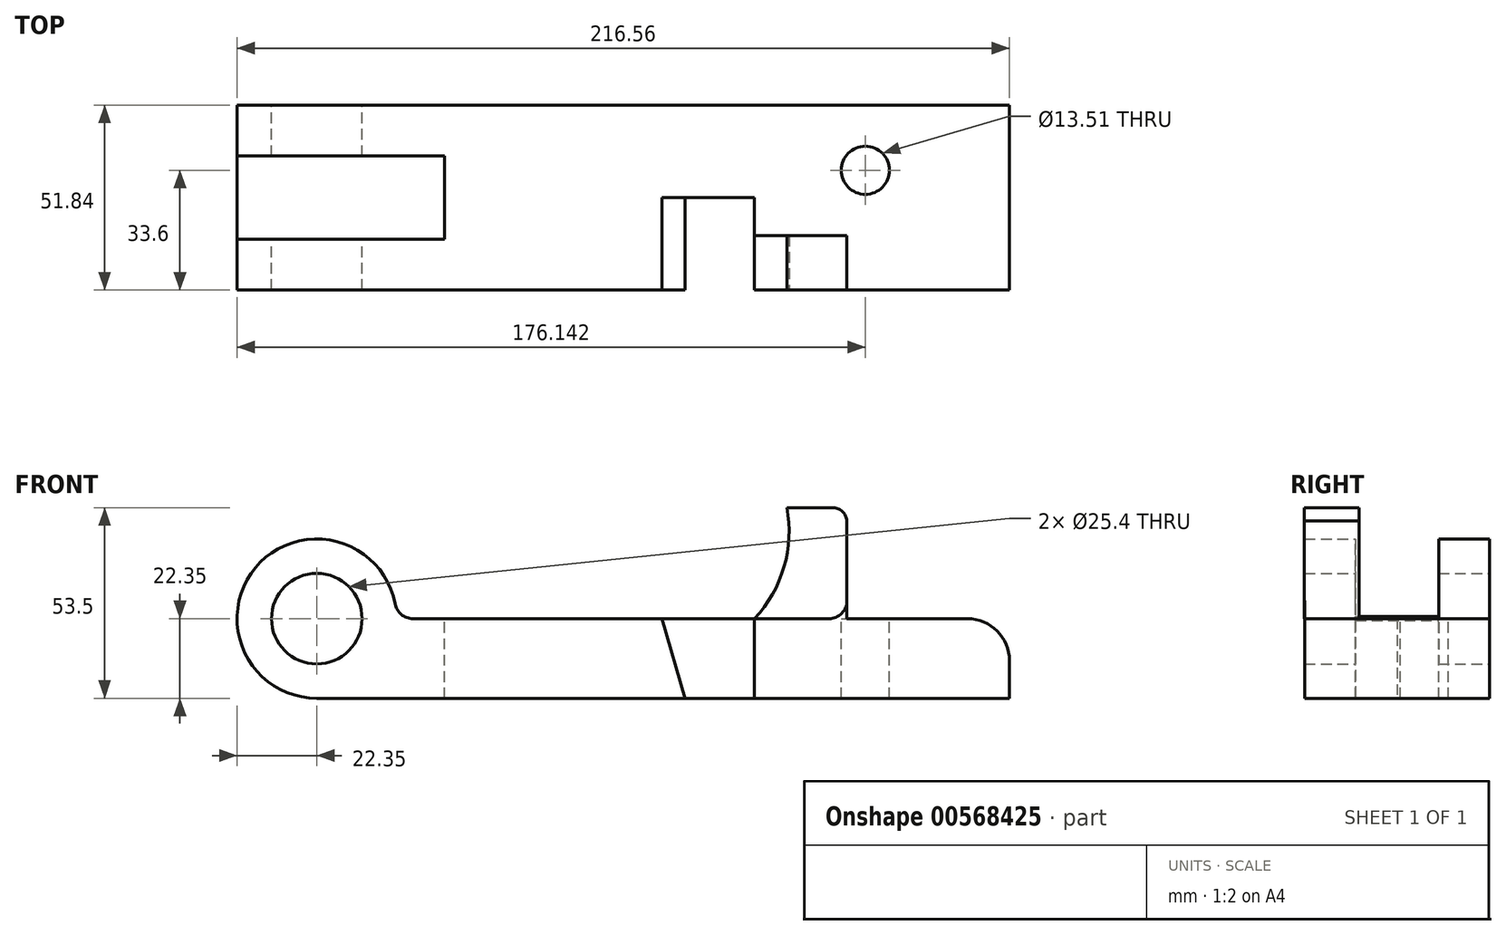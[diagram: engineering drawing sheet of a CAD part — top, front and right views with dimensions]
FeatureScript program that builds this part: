
annotation { "Feature Type Name" : "Feature", "Feature Type Description" : "" }
export const myFeature = defineFeature(function(context is Context, id is Id, definition is map)
    precondition{}
    {
        {
            var Q0;
            Q0=qCreatedBy(makeId("Front.planeOp"),FACE);
            var sketch = newSketch(context, id + "F0", { "sketchPlane" : qUnion([Q0])});
            skCircle(sketch, "E0", {"center": v(0, 0) * mm, "radius": 12.7 * mm});
            skArc(sketch, "E1", {"start": v(22.35, 0) * mm, "mid": v(-15.8, 15.8) * mm, "end": v(0, -22.35) * mm});
            skLineSegment(sketch, "E2", {"start": v(22.35, 0) * mm, "end": v(182.41, 0) * mm});
            skLineSegment(sketch, "E3", {"start": v(0, -22.35) * mm, "end": v(194.2, -22.35) * mm});
            skLineSegment(sketch, "E4", {"start": v(194.2, -22.35) * mm, "end": v(194.2, -11.8) * mm});
            skArc(sketch, "E5", {"start": v(182.41, 0) * mm, "mid": v(190.75, -3.46) * mm, "end": v(194.2, -11.8) * mm});
            skSolve(sketch);
        }
        {
            var Q0;
            Q0=qCreatedBy(makeId("Top.planeOp"),FACE);
            var sketch = newSketch(context, id + "F1", { "sketchPlane" : qUnion([Q0])});
            skLineSegment(sketch, "E6", {"start": v(-22.34, 0) * mm, "end": v(-22.34, -35.56) * mm});
            skLineSegment(sketch, "E7", {"start": v(-22.34, -35.56) * mm, "end": v(195.42, -35.56) * mm});
            skLineSegment(sketch, "E8", {"start": v(195.42, -35.56) * mm, "end": v(195.42, 35.56) * mm});
            skLineSegment(sketch, "E9", {"start": v(195.42, 35.56) * mm, "end": v(-22.34, 35.56) * mm});
            skLineSegment(sketch, "E10", {"start": v(-22.34, 35.56) * mm, "end": v(-22.34, 0) * mm});
            skLineSegment(sketch, "E11", {"start": v(-22.34, -11.66) * mm, "end": v(35.79, -11.66) * mm});
            skLineSegment(sketch, "E12", {"start": v(35.79, -11.66) * mm, "end": v(35.79, 11.66) * mm});
            skLineSegment(sketch, "E13", {"start": v(35.79, 11.66) * mm, "end": v(-22.34, 11.66) * mm});
            skLineSegment(sketch, "E14", {"start": v(-22.34, 11.66) * mm, "end": v(-22.34, -11.66) * mm});
            skSolve(sketch);
        }
        {
            var Q0;
            Q0=qCreatedBy(makeId("Front.planeOp"),FACE);
            cPlane(context, id + "F2", {"entities" : qUnion([Q0]), "cplaneType" : CPlaneType.OFFSET, "offset" : 25.4 * mm, "width" : 152.4 * mm, "height" : 152.4 * mm});
        }
        {
            var Q0;
            Q0=qCreatedBy(id+"F2.planeOp",FACE);
            var sketch = newSketch(context, id + "F3", { "sketchPlane" : qUnion([Q0])});
            skLineSegment(sketch, "E15", {"start": v(122.73, 0) * mm, "end": v(122.73, -22.33) * mm});
            skLineSegment(sketch, "E16", {"start": v(122.73, -22.33) * mm, "end": v(97.5, -22.33) * mm});
            skLineSegment(sketch, "E17", {"start": v(97.5, -22.33) * mm, "end": v(92.37, 0) * mm});
            skLineSegment(sketch, "E18", {"start": v(92.37, 0) * mm, "end": v(122.73, 0) * mm});
            skLineSegment(sketch, "E19", {"start": v(122.73, 0) * mm, "end": v(148.65, 0) * mm});
            skLineSegment(sketch, "E20", {"start": v(148.65, 0) * mm, "end": v(148.65, 27.38) * mm});
            skLineSegment(sketch, "E21", {"start": v(144.54, 31.15) * mm, "end": v(131.81, 31.15) * mm});
            skArc(sketch, "E22", {"start": v(144.54, 31.15) * mm, "mid": v(147.33, 30.06) * mm, "end": v(148.65, 27.38) * mm});
            skArc(sketch, "E23", {"start": v(122.73, 0) * mm, "mid": v(131, 14.5) * mm, "end": v(131.81, 31.15) * mm});
            skSolve(sketch);
        }
        {
            var Q0;
            Q0 = qSketchRegion(id + "F0", true);
            extrude(context, id + "F4", {"entities" : qUnion([Q0]), "endBound" : BoundingType.SYMMETRIC, "depth" : 51.82 * mm, "offsetDistance" : 25.4 * mm});
        }
        {
            var Q0;
            Q0=makeQuery(id+"F3.imprint","IMPRINT",FACE,{"disambiguationData":[TD([[makeQuery(id+"F3.imprint","IMPRINT",EDGE,{"derivedFrom":sQuery(id+"F3.wireOp",EDGE,"E19")}),1.0]])]});
            extrude(context, id + "F5", {"entities" : qUnion([Q0]), "operationType" : NewBodyOperationType.ADD, "oppositeDirection" : true, "depth" : 14.73 * mm, "offsetDistance" : 25.4 * mm, "hasSecondDirection" : true, "secondDirectionOppositeDirection" : false, "secondDirectionDepth" : 0.53 * mm});
        }
        {
            var Q0;
            Q0=makeQuery(id+"F1.imprint","IMPRINT",FACE,{"disambiguationData":[TD([[makeQuery(id+"F1.imprint","IMPRINT",EDGE,{"derivedFrom":sQuery(id+"F1.wireOp",EDGE,"E11")}),1.0]])]});
            extrude(context, id + "F6", {"entities" : qUnion([Q0]), "operationType" : NewBodyOperationType.REMOVE, "endBound" : BoundingType.SYMMETRIC, "oppositeDirection" : true, "depth" : 103.63 * mm, "offsetDistance" : 25.4 * mm});
        }
        {
            var Q0;
            Q0=qCreatedBy(makeId("Top.planeOp"),FACE);
            var sketch = newSketch(context, id + "F7", { "sketchPlane" : qUnion([Q0])});
            skCircle(sketch, "E24", {"center": v(153.8, 7.67) * mm, "radius": 6.76 * mm});
            skSolve(sketch);
        }
        {
            var Q0;
            Q0=makeQuery(id+"F7.imprint","IMPRINT",FACE,{"disambiguationData":[TD([[makeQuery(id+"F7.imprint","IMPRINT",EDGE,{"derivedFrom":sQuery(id+"F7.wireOp",EDGE,"E24")}),1.0]])]});
            var Q1;
            Q1=sQuery(id+"F7.wireOp",EDGE,"E24");
            extrude(context, id + "F8", {"entities" : qUnion([Q0]), "operationType" : NewBodyOperationType.REMOVE, "surfaceEntities" : qUnion([Q1]), "oppositeDirection" : true, "depth" : 76.45 * mm, "offsetDistance" : 25.4 * mm});
        }
        {
            var Q0;
            Q0=qCreatedBy(makeId("Front.planeOp"),FACE);
            var sketch = newSketch(context, id + "F9", { "sketchPlane" : qUnion([Q0])});
            skLineSegment(sketch, "E25", {"start": v(122.73, 0) * mm, "end": v(122.73, -22.42) * mm});
            skLineSegment(sketch, "E26", {"start": v(122.73, -22.42) * mm, "end": v(103.25, -22.42) * mm});
            skLineSegment(sketch, "E27", {"start": v(103.25, -22.42) * mm, "end": v(96.77, 0) * mm});
            skLineSegment(sketch, "E28", {"start": v(96.77, 0) * mm, "end": v(122.73, 0) * mm});
            skSolve(sketch);
        }
        {
            var Q0;
            Q0 = qSketchRegion(id + "F9", true);
            extrude(context, id + "F10", {"entities" : qUnion([Q0]), "operationType" : NewBodyOperationType.REMOVE, "depth" : 115.57 * mm, "offsetDistance" : 25.4 * mm});
        }
        {
            var Q0;
            {var subQ0=sQuery(id+"F0.wireOp",EDGE,"E2");var subQ1=sQuery(id+"F0.wireOp",EDGE,"E1");Q0=makeQuery(id+"F6.boolean.opBoolean","SPLIT",EDGE,{"disambiguationData":[TD([makeQuery(id+"F6.opExtrude","SWEPT_FACE",FACE,{"disambiguationData":[OSD([sQuery(id+"F1.wireOp",EDGE,"E11")])]})])],"derivedFrom":makeQuery(id+"F4.opExtrude","SWEPT_EDGE",EDGE,{"disambiguationData":[OSD([subQ1,subQ0])]})});}
            var Q1;
            {var subQ0=sQuery(id+"F0.wireOp",EDGE,"E2");var subQ1=sQuery(id+"F0.wireOp",EDGE,"E1");Q1=makeQuery(id+"F6.boolean.opBoolean","SPLIT",EDGE,{"disambiguationData":[TD([makeQuery(id+"F6.opExtrude","SWEPT_FACE",FACE,{"disambiguationData":[OSD([sQuery(id+"F1.wireOp",EDGE,"E13")])]})])],"derivedFrom":makeQuery(id+"F4.opExtrude","SWEPT_EDGE",EDGE,{"disambiguationData":[OSD([subQ1,subQ0])]})});}
            var Q2;
            {var subQ0=sQuery(id+"F3.wireOp",EDGE,"E20");Q2=makeQuery(id+"F5.boolean.opBoolean","SPLIT",EDGE,{"disambiguationData":[topologyDisambiguationEdgeConnected([makeQuery(id+"F4.opExtrude","SWEPT_FACE",FACE,{"disambiguationData":[OSD([sQuery(id+"F0.wireOp",EDGE,"E2")])]})])],"derivedFrom":makeQuery(id+"F5.opExtrude","SWEPT_EDGE",EDGE,{"disambiguationData":[OSD([sQuery(id+"F3.wireOp",EDGE,"E19"),subQ0])]})});}
            fillet(context, id + "F11", {"entities" : qUnion([Q0, Q1, Q2]), "radius" : 5.08 * mm, "tangentPropagation" : true, "allowEdgeOverflow" : false});
        }
    });
